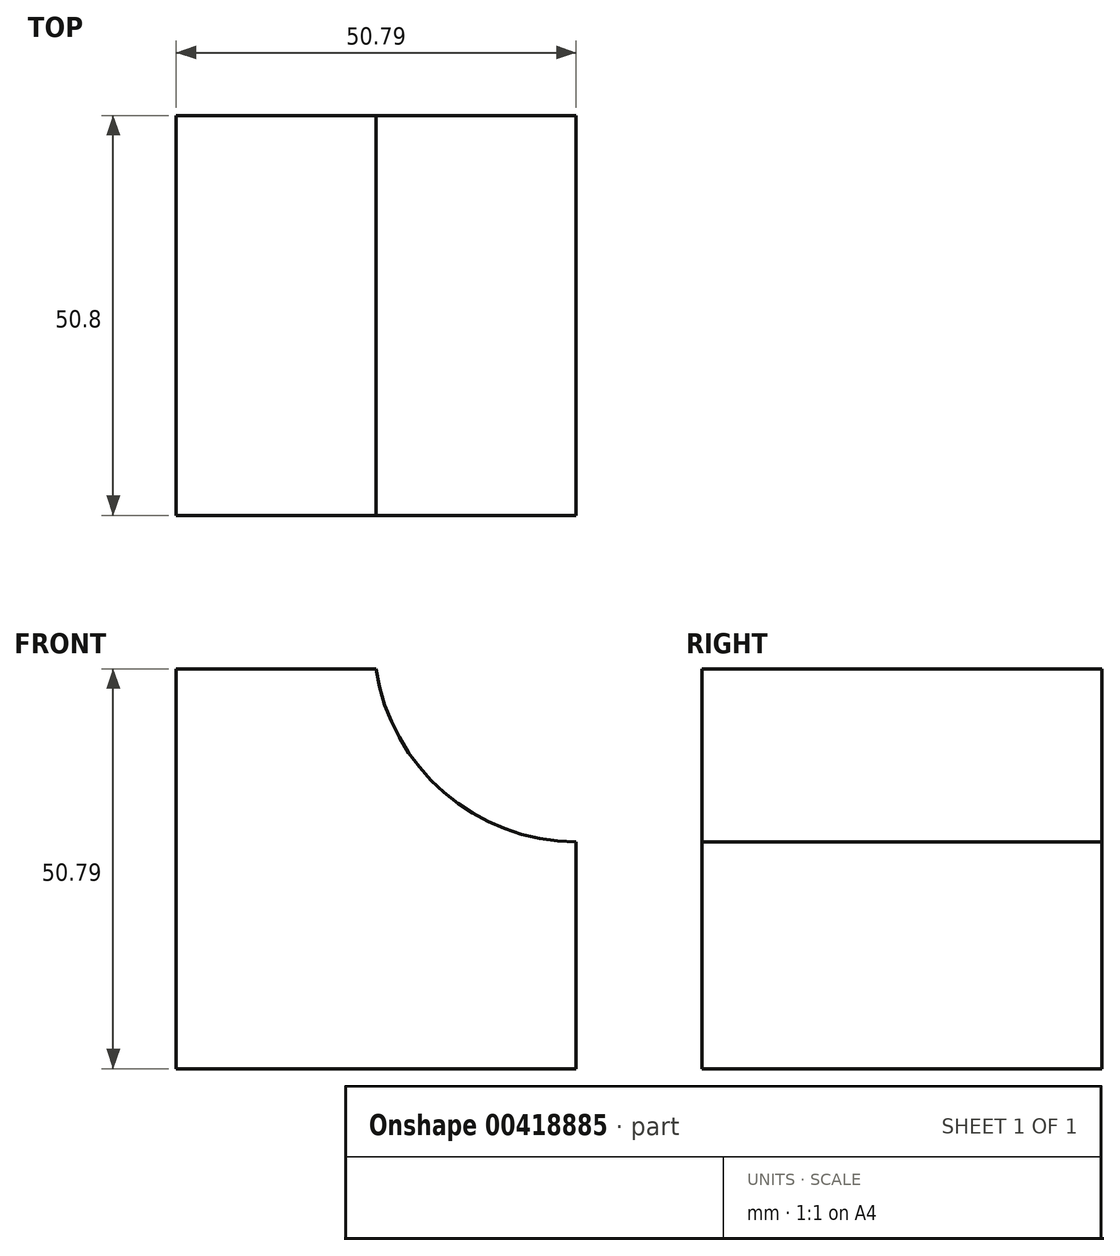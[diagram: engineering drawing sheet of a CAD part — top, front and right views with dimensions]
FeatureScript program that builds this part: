
annotation { "Feature Type Name" : "Feature", "Feature Type Description" : "" }
export const myFeature = defineFeature(function(context is Context, id is Id, definition is map)
    precondition{}
    {
        {
            var Q0;
            Q0=qCreatedBy(makeId("Front.planeOp"),FACE);
            var sketch = newSketch(context, id + "F0", { "sketchPlane" : qUnion([Q0])});
            skLineSegment(sketch, "E0", {"start": v(0, 0) * mm, "end": v(-50.8, 0) * mm});
            skLineSegment(sketch, "E1", {"start": v(-50.8, 0) * mm, "end": v(-50.8, 50.8) * mm});
            skLineSegment(sketch, "E2", {"start": v(-50.8, 50.8) * mm, "end": v(-25.4, 50.8) * mm});
            skLineSegment(sketch, "E3", {"start": v(0, 28.83) * mm, "end": v(0, 0) * mm});
            skArc(sketch, "E4", {"start": v(-25.4, 50.8) * mm, "mid": v(-16.79, 35.09) * mm, "end": v(0, 28.83) * mm});
            skSolve(sketch);
        }
        {
            var Q0;
            Q0 = qSketchRegion(id + "F0", true);
            extrude(context, id + "F1", {"entities" : qUnion([Q0]), "depth" : 50.8 * mm});
        }
    });
